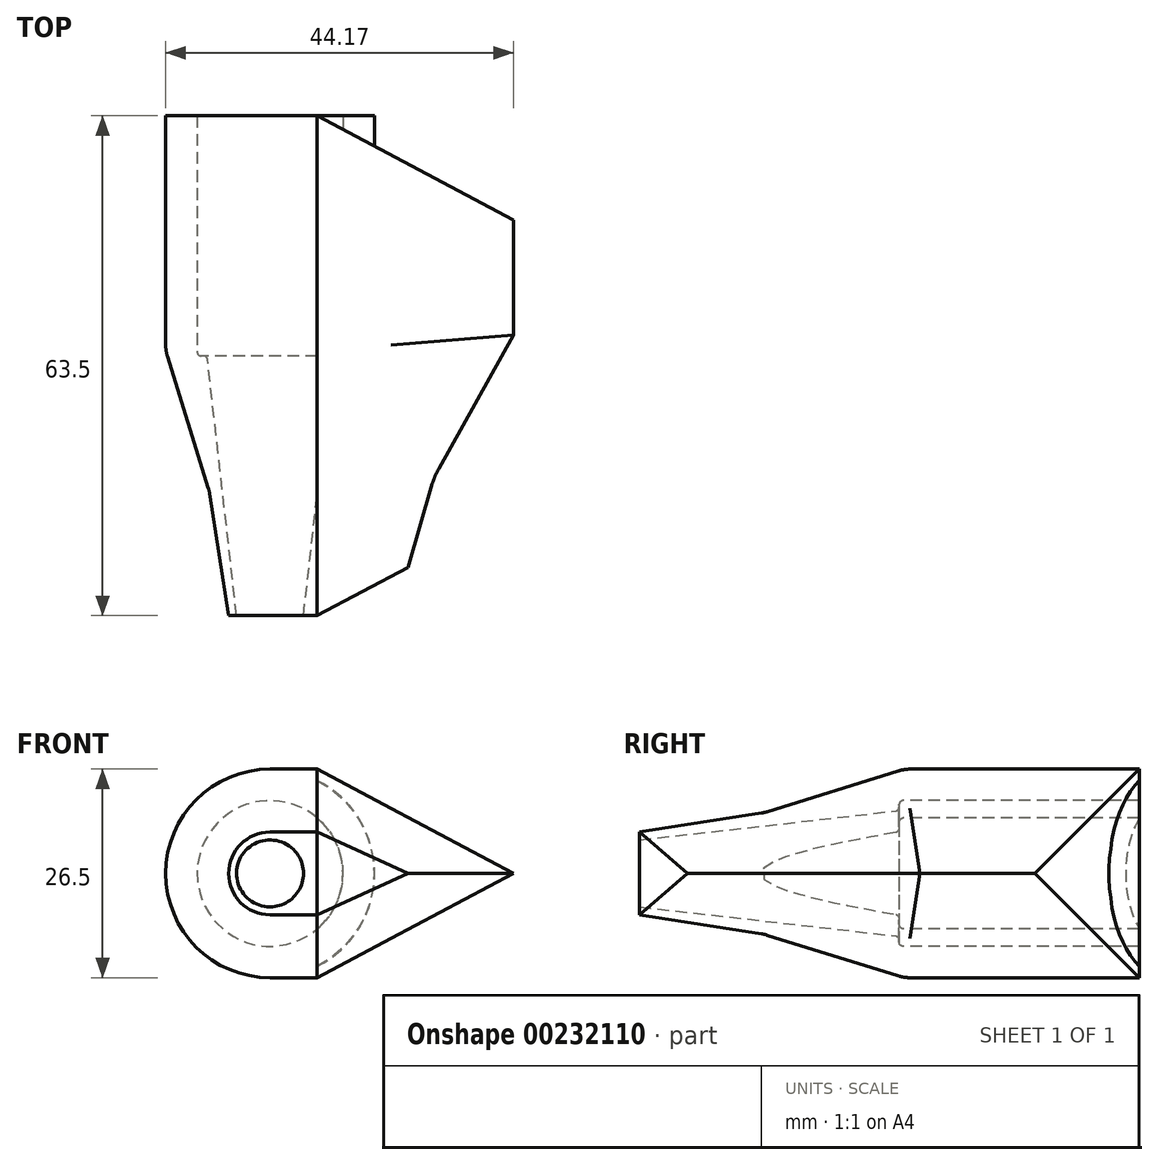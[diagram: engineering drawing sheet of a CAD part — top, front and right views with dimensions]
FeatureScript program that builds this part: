
annotation { "Feature Type Name" : "Feature", "Feature Type Description" : "" }
export const myFeature = defineFeature(function(context is Context, id is Id, definition is map)
    precondition{}
    {
        {
            var Q0;
            Q0=qCreatedBy(makeId("Top.planeOp"),FACE);
            var sketch = newSketch(context, id + "F0", { "sketchPlane" : qUnion([Q0])});
            skLineSegment(sketch, "E0", {"start": v(0, 0) * mm, "end": v(4.25, 0) * mm, "construction": true});
            skLineSegment(sketch, "E1", {"start": v(4.25, 0) * mm, "end": v(5.25, 0) * mm});
            skLineSegment(sketch, "E2", {"start": v(4.25, 0) * mm, "end": v(4.25, 33) * mm, "construction": true});
            skLineSegment(sketch, "E3", {"start": v(4.74, 33) * mm, "end": v(7.99, 33) * mm, "construction": true});
            skLineSegment(sketch, "E4", {"start": v(8.43, 33) * mm, "end": v(8.75, 33) * mm});
            skLineSegment(sketch, "E5", {"start": v(7.67, 15.52) * mm, "end": v(5.25, 0) * mm});
            skLineSegment(sketch, "E6", {"start": v(7.94, 32.56) * mm, "end": v(4.25, 0) * mm});
            skLineSegment(sketch, "E7", {"start": v(0, 33) * mm, "end": v(9.25, 33) * mm, "construction": true});
            skPoint(sketch, "E7.endSnap0", {"position": v(9.2, 33) * mm});
            skLineSegment(sketch, "E8", {"start": v(9.25, 33.5) * mm, "end": v(9.25, 63.5) * mm});
            skLineSegment(sketch, "E9", {"start": v(9.25, 63.5) * mm, "end": v(13.25, 63.5) * mm});
            skLineSegment(sketch, "E10", {"start": v(13.25, 34.4) * mm, "end": v(13.25, 63.5) * mm});
            skPoint(sketch, "E11.visualSharp", {"position": v(9.25, 33) * mm});
            skArc(sketch, "E11.filletArc", {"start": v(8.75, 33) * mm, "mid": v(9.1, 33.15) * mm, "end": v(9.25, 33.5) * mm});
            skPoint(sketch, "E12.visualSharp", {"position": v(10.4, 33) * mm});
            skPoint(sketch, "E13.visualSharp", {"position": v(7.99, 33) * mm});
            skArc(sketch, "E13.filletArc", {"start": v(8.43, 33) * mm, "mid": v(8.1, 32.87) * mm, "end": v(7.94, 32.56) * mm});
            skLineSegment(sketch, "E14", {"start": v(7.84, 16.23) * mm, "end": v(13.02, 32.9) * mm});
            skPoint(sketch, "E15.visualSharp", {"position": v(13.25, 33.63) * mm});
            skArc(sketch, "E15.filletArc", {"start": v(13.02, 32.9) * mm, "mid": v(13.2, 33.64) * mm, "end": v(13.25, 34.4) * mm});
            skPoint(sketch, "E16.visualSharp", {"position": v(7.73, 15.88) * mm});
            skArc(sketch, "E16.filletArc", {"start": v(7.84, 16.23) * mm, "mid": v(7.74, 15.88) * mm, "end": v(7.67, 15.52) * mm});
            skLineSegment(sketch, "E17", {"start": v(0, 0) * mm, "end": v(0, 65) * mm, "construction": true});
            skSolve(sketch);
        }
        {
            var Q0;
            Q0=makeQuery(id+"F0.imprint","IMPRINT",FACE,{"disambiguationData":[TD([[makeQuery(id+"F0.imprint","IMPRINT",EDGE,{"derivedFrom":sQuery(id+"F0.wireOp",EDGE,"E1")}),1.0]])]});
            var Q1;
            Q1=sQuery(id+"F0.wireOp",EDGE,"E17");
            revolve(context, id + "F1", {"entities" : qUnion([Q0]), "axis" : qUnion([Q1]), "revolveType" : RevolveType.FULL});
        }
        {
            var Q0;
            Q0=qCreatedBy(makeId("Right.planeOp"),FACE);
            var sketch = newSketch(context, id + "F2", { "sketchPlane" : qUnion([Q0])});
            skLineSegment(sketch, "E18", {"start": v(0, 5.25) * mm, "end": v(15.52, 7.67) * mm});
            skLineSegment(sketch, "E19", {"start": v(15.52, -7.67) * mm, "end": v(0, -5.25) * mm});
            skArc(sketch, "E20", {"start": v(16.23, -7.84) * mm, "mid": v(15.88, -7.74) * mm, "end": v(15.52, -7.67) * mm});
            skArc(sketch, "E21", {"start": v(15.52, 7.67) * mm, "mid": v(15.88, 7.74) * mm, "end": v(16.23, 7.84) * mm});
            skLineSegment(sketch, "E22", {"start": v(32.9, 13.02) * mm, "end": v(16.23, 7.84) * mm});
            skLineSegment(sketch, "E23", {"start": v(16.23, -7.84) * mm, "end": v(32.9, -13.02) * mm});
            skArc(sketch, "E24", {"start": v(32.9, -13.02) * mm, "mid": v(33.64, -13.2) * mm, "end": v(34.4, -13.25) * mm});
            skArc(sketch, "E25", {"start": v(34.4, 13.25) * mm, "mid": v(33.64, 13.2) * mm, "end": v(32.9, 13.02) * mm});
            skLineSegment(sketch, "E26", {"start": v(34.4, -13.25) * mm, "end": v(63.5, -13.25) * mm});
            skLineSegment(sketch, "E27", {"start": v(63.5, 13.25) * mm, "end": v(34.4, 13.25) * mm});
            skLineSegment(sketch, "E28", {"start": v(0, 5.25) * mm, "end": v(0, -5.25) * mm});
            skLineSegment(sketch, "E29", {"start": v(63.5, 13.25) * mm, "end": v(63.5, -13.25) * mm});
            skSolve(sketch);
        }
        {
            var Q0;
            Q0=qSketchRegion(id+"F2",true);
            extrude(context, id + "F3", {"entities" : qUnion([Q0]), "operationType" : NewBodyOperationType.ADD, "depth" : 6 * mm});
        }
        {
            var Q0;
            Q0=makeQuery(id+"F3.opExtrude","CAP_FACE",FACE,{"disambiguationData":[OSD([sQuery(id+"F2.wireOp",EDGE,"E18"),sQuery(id+"F2.wireOp",EDGE,"E19"),sQuery(id+"F2.wireOp",EDGE,"E20"),sQuery(id+"F2.wireOp",EDGE,"E21"),sQuery(id+"F2.wireOp",EDGE,"E22"),sQuery(id+"F2.wireOp",EDGE,"E23"),sQuery(id+"F2.wireOp",EDGE,"E24"),sQuery(id+"F2.wireOp",EDGE,"E25"),sQuery(id+"F2.wireOp",EDGE,"E26"),sQuery(id+"F2.wireOp",EDGE,"E27"),sQuery(id+"F2.wireOp",EDGE,"E28"),sQuery(id+"F2.wireOp",EDGE,"E29")])],"isStart":true});
            var sketch = newSketch(context, id + "F4", { "sketchPlane" : qUnion([Q0])});
            skLineSegment(sketch, "E30.0.0", {"start": v(-63.5, 0) * mm, "end": v(-63.5, -9.25) * mm});
            skLineSegment(sketch, "E30.0.1", {"start": v(-63.5, -9.25) * mm, "end": v(-33.5, -9.25) * mm});
            skArc(sketch, "E30.0.2", {"start": v(-33.5, -9.25) * mm, "mid": v(-33.15, -9.1) * mm, "end": v(-33, -8.75) * mm});
            skLineSegment(sketch, "E30.0.3", {"start": v(-33, -8.75) * mm, "end": v(-33, -8.43) * mm});
            skArc(sketch, "E30.0.4", {"start": v(-32.56, -7.94) * mm, "mid": v(-32.87, -8.1) * mm, "end": v(-33, -8.43) * mm});
            skLineSegment(sketch, "E30.0.5", {"start": v(-32.56, -7.94) * mm, "end": v(0, -4.25) * mm});
            skLineSegment(sketch, "E30.0.6", {"start": v(0, -4.25) * mm, "end": v(0, 0) * mm});
            skPoint(sketch, "E30.0.11.end.orphan", {"position": v(-63.5, 9.25) * mm});
            skPoint(sketch, "E30.0.10.end.orphan", {"position": v(-33.5, 9.25) * mm});
            skPoint(sketch, "E30.0.9.end.orphan", {"position": v(-33, 8.75) * mm});
            skPoint(sketch, "E30.0.8.start.orphan", {"position": v(-33, 8.43) * mm});
            skPoint(sketch, "E30.0.7.end.orphan", {"position": v(-32.56, 7.94) * mm});
            skPoint(sketch, "E31.orphan", {"position": v(0, 4.25) * mm});
            skLineSegment(sketch, "E32", {"start": v(0, 0) * mm, "end": v(-63.5, 0) * mm});
            skSolve(sketch);
        }
        {
            var Q0;
            Q0=qSketchRegion(id+"F4",true);
            var Q1;
            Q1=sQuery(id+"F4.wireOp",EDGE,"E32");
            revolve(context, id + "F5", {"operationType" : NewBodyOperationType.REMOVE, "entities" : qUnion([Q0]), "axis" : qUnion([Q1]), "revolveType" : RevolveType.FULL});
        }
        {
            var Q0;
            {var subQ0=sQuery(id+"F2.wireOp",EDGE,"E19");var subQ1=sQuery(id+"F2.wireOp",EDGE,"E29");var subQ2=sQuery(id+"F2.wireOp",EDGE,"E20");var subQ3=sQuery(id+"F2.wireOp",EDGE,"E18");var subQ4=sQuery(id+"F2.wireOp",EDGE,"E23");var subQ5=sQuery(id+"F2.wireOp",EDGE,"E26");var subQ6=sQuery(id+"F2.wireOp",EDGE,"E21");var subQ7=sQuery(id+"F2.wireOp",EDGE,"E22");var subQ8=sQuery(id+"F2.wireOp",EDGE,"E24");var subQ9=sQuery(id+"F2.wireOp",EDGE,"E25");var subQ10=sQuery(id+"F2.wireOp",EDGE,"E27");var subQ11=sQuery(id+"F2.wireOp",EDGE,"E28");Q0=makeQuery(id+"F3.boolean.opBoolean","SPLIT",FACE,{"disambiguationData":[TD([makeQuery(id+"F1.opRevolve","SWEPT_FACE",FACE,{"disambiguationData":[OSD([sQuery(id+"F0.wireOp",EDGE,"E1")])]})])],"derivedFrom":makeQuery(id+"F3.opExtrude","CAP_FACE",FACE,{"disambiguationData":[OSD([subQ3,subQ0,subQ2,subQ6,subQ7,subQ4,subQ8,subQ9,subQ5,subQ10,subQ11,subQ1])],"isStart":false})});}
            var sketch = newSketch(context, id + "F6", { "sketchPlane" : qUnion([Q0])});
            skLineSegment(sketch, "E33.0.11", {"start": v(63.5, 13.25) * mm, "end": v(34.4, 13.25) * mm});
            skArc(sketch, "E33.0.12", {"start": v(34.4, 13.25) * mm, "mid": v(33.64, 13.2) * mm, "end": v(32.9, 13.02) * mm});
            skLineSegment(sketch, "E33.0.13", {"start": v(32.9, 13.02) * mm, "end": v(16.23, 7.84) * mm});
            skArc(sketch, "E33.0.14", {"start": v(16.23, 7.84) * mm, "mid": v(15.88, 7.74) * mm, "end": v(15.52, 7.67) * mm});
            skLineSegment(sketch, "E33.0.15", {"start": v(15.52, 7.67) * mm, "end": v(0, 5.25) * mm});
            skLineSegment(sketch, "E33.0.16", {"start": v(0, 5.25) * mm, "end": v(0, -5.25) * mm});
            skLineSegment(sketch, "E33.0.17", {"start": v(0, -5.25) * mm, "end": v(15.52, -7.67) * mm});
            skArc(sketch, "E33.0.18", {"start": v(15.52, -7.67) * mm, "mid": v(15.88, -7.74) * mm, "end": v(16.23, -7.84) * mm});
            skLineSegment(sketch, "E33.0.19", {"start": v(16.23, -7.84) * mm, "end": v(32.9, -13.02) * mm});
            skArc(sketch, "E33.0.20", {"start": v(32.9, -13.02) * mm, "mid": v(33.64, -13.2) * mm, "end": v(34.4, -13.25) * mm});
            skLineSegment(sketch, "E33.0.21", {"start": v(34.4, -13.25) * mm, "end": v(63.5, -13.25) * mm});
            skPoint(sketch, "E33.0.5.start.orphan", {"position": v(15.52, 4.78) * mm});
            skPoint(sketch, "E33.0.6.end.orphan", {"position": v(16.23, 5.04) * mm});
            skPoint(sketch, "E33.0.6.start.orphan", {"position": v(15.52, 4.78) * mm});
            skPoint(sketch, "E33.0.7.end.orphan", {"position": v(32.9, 11.56) * mm});
            skPoint(sketch, "E33.0.7.start.orphan", {"position": v(16.23, 5.04) * mm});
            skPoint(sketch, "E33.0.8.start.orphan", {"position": v(32.9, 11.56) * mm});
            skPoint(sketch, "E33.0.9.start.orphan", {"position": v(34.4, 11.81) * mm});
            skPoint(sketch, "E33.0.4.end.orphan", {"position": v(15.52, -4.78) * mm});
            skPoint(sketch, "E33.0.4.start.orphan", {"position": v(16.23, -5.04) * mm});
            skPoint(sketch, "E33.0.2.end.orphan", {"position": v(32.9, -11.56) * mm});
            skPoint(sketch, "E33.0.2.start.orphan", {"position": v(34.4, -11.81) * mm});
            skPoint(sketch, "E33.0.1.end.orphan", {"position": v(34.4, -11.81) * mm});
            skPoint(sketch, "E33.0.10.start.orphan", {"position": v(63.5, 11.81) * mm});
            skPoint(sketch, "E33.0.0.end.orphan", {"position": v(63.5, -11.81) * mm});
            skLineSegment(sketch, "E34", {"start": v(63.5, 13.25) * mm, "end": v(63.5, -13.25) * mm});
            skSolve(sketch);
        }
        {
            var Q0;
            Q0=qSketchRegion(id+"F6",true);
            extrude(context, id + "F7", {"entities" : qUnion([Q0]), "operationType" : NewBodyOperationType.ADD, "depth" : 25 * mm, "hasDraft" : true, "draftAngle" : 28 * degree, "draftPullDirection" : true});
        }
    });
